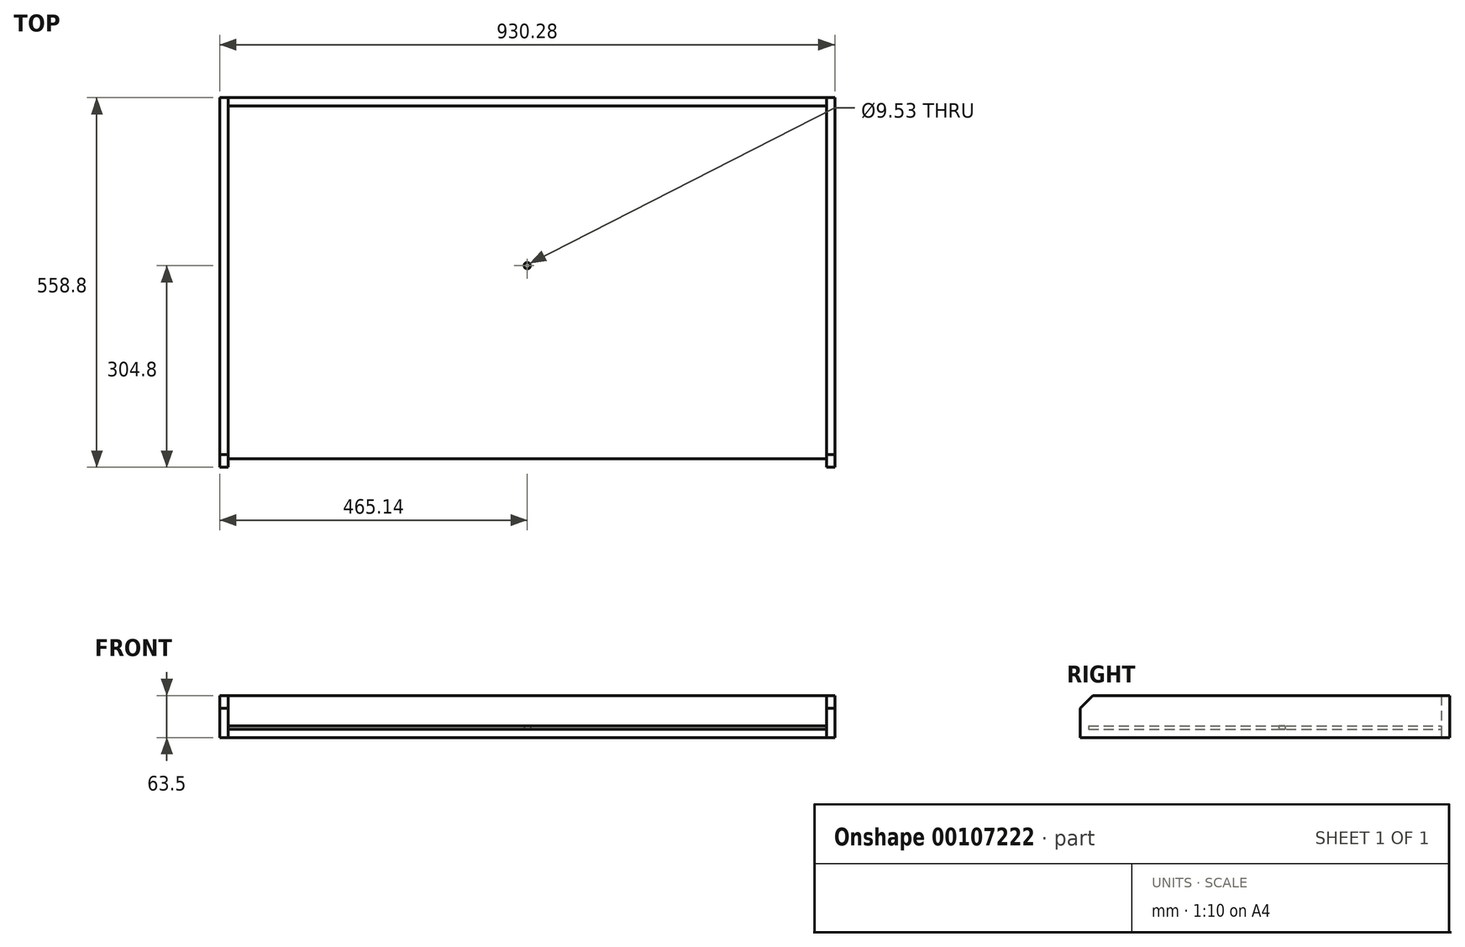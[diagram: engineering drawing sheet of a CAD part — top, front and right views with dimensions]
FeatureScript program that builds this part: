
annotation { "Feature Type Name" : "Feature", "Feature Type Description" : "" }
export const myFeature = defineFeature(function(context is Context, id is Id, definition is map)
    precondition{}
    {
        {
            var Q0;
            Q0=qCreatedBy(makeId("Right.planeOp"),FACE);
            var sketch = newSketch(context, id + "F0", { "sketchPlane" : qUnion([Q0])});
            skLineSegment(sketch, "E0.bottom", {"start": v(0, 63.5) * mm, "end": v(558.8, 63.5) * mm});
            skLineSegment(sketch, "E0.top", {"start": v(0, 0) * mm, "end": v(558.8, 0) * mm});
            skLineSegment(sketch, "E0.left", {"start": v(0, 63.5) * mm, "end": v(0, 0) * mm});
            skLineSegment(sketch, "E0.right", {"start": v(558.8, 63.5) * mm, "end": v(558.8, 0) * mm});
            skSolve(sketch);
        }
        {
            var Q0;
            Q0=makeQuery(id+"F0.imprint","IMPRINT",FACE,{"disambiguationData":[TD([[makeQuery(id+"F0.imprint","IMPRINT",EDGE,{"derivedFrom":sQuery(id+"F0.wireOp",EDGE,"E0.bottom")}),-1.0]])]});
            extrude(context, id + "F1", {"entities" : qUnion([Q0]), "depth" : 12.7 * mm});
        }
        {
            var Q0;
            Q0=makeQuery(id+"F1.opExtrude","SWEPT_EDGE",EDGE,{"disambiguationData":[OSD([sQuery(id+"F0.wireOp",EDGE,"E0.bottom"),sQuery(id+"F0.wireOp",EDGE,"E0.left")])]});
            chamfer(context, id + "F2", {"entities" : qUnion([Q0]), "width" : 19.05 * mm, "tangentPropagation" : true});
        }
        {
            var Q0;
            Q0=makeQuery(id+"F1.opExtrude","SWEPT_BODY",BODY,{"disambiguationData":[OSD([sQuery(id+"F0.wireOp",EDGE,"E0.bottom"),sQuery(id+"F0.wireOp",EDGE,"E0.top"),sQuery(id+"F0.wireOp",EDGE,"E0.left"),sQuery(id+"F0.wireOp",EDGE,"E0.right")])]});
            transform(context, id + "F3", {"entities" : qUnion([Q0]), "transformType" : TransformType.TRANSLATION_3D, "dx" : -465.14 * mm, "dy" : 0 * mm, "dz" : 0 * mm, "makeCopy" : false});
        }
        {
            var Q0;
            Q0=qCreatedBy(makeId("Top.planeOp"),FACE);
            var sketch = newSketch(context, id + "F4", { "sketchPlane" : qUnion([Q0])});
            skLineSegment(sketch, "E1.bottom", {"start": v(-452.44, 558.8) * mm, "end": v(452.44, 558.8) * mm});
            skLineSegment(sketch, "E1.top", {"start": v(-452.44, 546.1) * mm, "end": v(452.44, 546.1) * mm});
            skLineSegment(sketch, "E1.left", {"start": v(-452.44, 558.8) * mm, "end": v(-452.44, 546.1) * mm});
            skLineSegment(sketch, "E1.right", {"start": v(452.44, 558.8) * mm, "end": v(452.44, 546.1) * mm});
            skLineSegment(sketch, "E2", {"start": v(0, 558.8) * mm, "end": v(0, 0) * mm, "construction": true});
            skSolve(sketch);
        }
        {
            var Q0;
            Q0 = qSketchRegion(id + "F4", true);
            extrude(context, id + "F5", {"entities" : qUnion([Q0]), "depth" : 63.5 * mm});
        }
        {
            var Q0;
            Q0=makeQuery(id+"F1.opExtrude","SWEPT_BODY",BODY,{"disambiguationData":[OSD([sQuery(id+"F0.wireOp",EDGE,"E0.bottom"),sQuery(id+"F0.wireOp",EDGE,"E0.top"),sQuery(id+"F0.wireOp",EDGE,"E0.left"),sQuery(id+"F0.wireOp",EDGE,"E0.right")])]});
            var Q1;
            Q1=qCreatedBy(makeId("Right.planeOp"),FACE);
            mirror(context, id + "F6", {"entities" : qUnion([Q0]), "mirrorPlane" : qUnion([Q1])});
        }
        {
            var Q0;
            Q0=qCreatedBy(makeId("Top.planeOp"),FACE);
            var sketch = newSketch(context, id + "F7", { "sketchPlane" : qUnion([Q0])});
            skLineSegment(sketch, "E3.bottom", {"start": v(-452.44, 12.7) * mm, "end": v(452.44, 12.7) * mm});
            skLineSegment(sketch, "E3.top", {"start": v(-452.44, 546.1) * mm, "end": v(452.44, 546.1) * mm});
            skLineSegment(sketch, "E3.left", {"start": v(-452.44, 12.7) * mm, "end": v(-452.44, 546.1) * mm});
            skLineSegment(sketch, "E3.right", {"start": v(452.44, 12.7) * mm, "end": v(452.44, 546.1) * mm});
            skLineSegment(sketch, "E4", {"start": v(0, 12.7) * mm, "end": v(0, 0) * mm, "construction": true});
            skSolve(sketch);
        }
        {
            var Q0;
            Q0 = qSketchRegion(id + "F7", true);
            extrude(context, id + "F8", {"entities" : qUnion([Q0]), "depth" : 4.76 * mm});
        }
        {
            var Q0;
            Q0=makeQuery(id+"F8.opExtrude","SWEPT_BODY",BODY,{"disambiguationData":[OSD([sQuery(id+"F7.wireOp",EDGE,"E3.bottom"),sQuery(id+"F7.wireOp",EDGE,"E3.top"),sQuery(id+"F7.wireOp",EDGE,"E3.left"),sQuery(id+"F7.wireOp",EDGE,"E3.right")])]});
            transform(context, id + "F9", {"entities" : qUnion([Q0]), "transformType" : TransformType.TRANSLATION_3D, "dx" : 0 * mm, "dy" : 0 * mm, "dz" : 12.7 * mm, "makeCopy" : false});
        }
        {
            var Q0;
            Q0=qCreatedBy(makeId("Top.planeOp"),FACE);
            var sketch = newSketch(context, id + "F10", { "sketchPlane" : qUnion([Q0])});
            skCircle(sketch, "E5", {"center": v(0, 304.8) * mm, "radius": 4.76 * mm});
            skLineSegment(sketch, "E6", {"start": v(0, 304.8) * mm, "end": v(0, 0) * mm, "construction": true});
            skLineSegment(sketch, "E7", {"start": v(0, 304.8) * mm, "end": v(-101.6, 304.8) * mm, "construction": true});
            skLineSegment(sketch, "E8", {"start": v(-101.6, 304.8) * mm, "end": v(-101.6, 558.8) * mm, "construction": true});
            skLineSegment(sketch, "E9", {"start": v(-101.6, 304.8) * mm, "end": v(-101.6, 50.8) * mm, "construction": true});
            skCircle(sketch, "E10", {"center": v(0, 304.8) * mm, "radius": 273.57 * mm, "construction": true});
            skSolve(sketch);
        }
        {
            var Q0;
            Q0=makeQuery(id+"F10.imprint","IMPRINT",FACE,{"disambiguationData":[TD([[makeQuery(id+"F10.imprint","IMPRINT",EDGE,{"derivedFrom":sQuery(id+"F10.wireOp",EDGE,"E5")}),1.0]])]});
            var Q1;
            Q1=sQuery(id+"F10.wireOp",EDGE,"E5");
            extrude(context, id + "F11", {"entities" : qUnion([Q0]), "operationType" : NewBodyOperationType.REMOVE, "surfaceEntities" : qUnion([Q1]), "endBound" : BoundingType.THROUGH_ALL, "depth" : 25.4 * mm});
        }
    });
